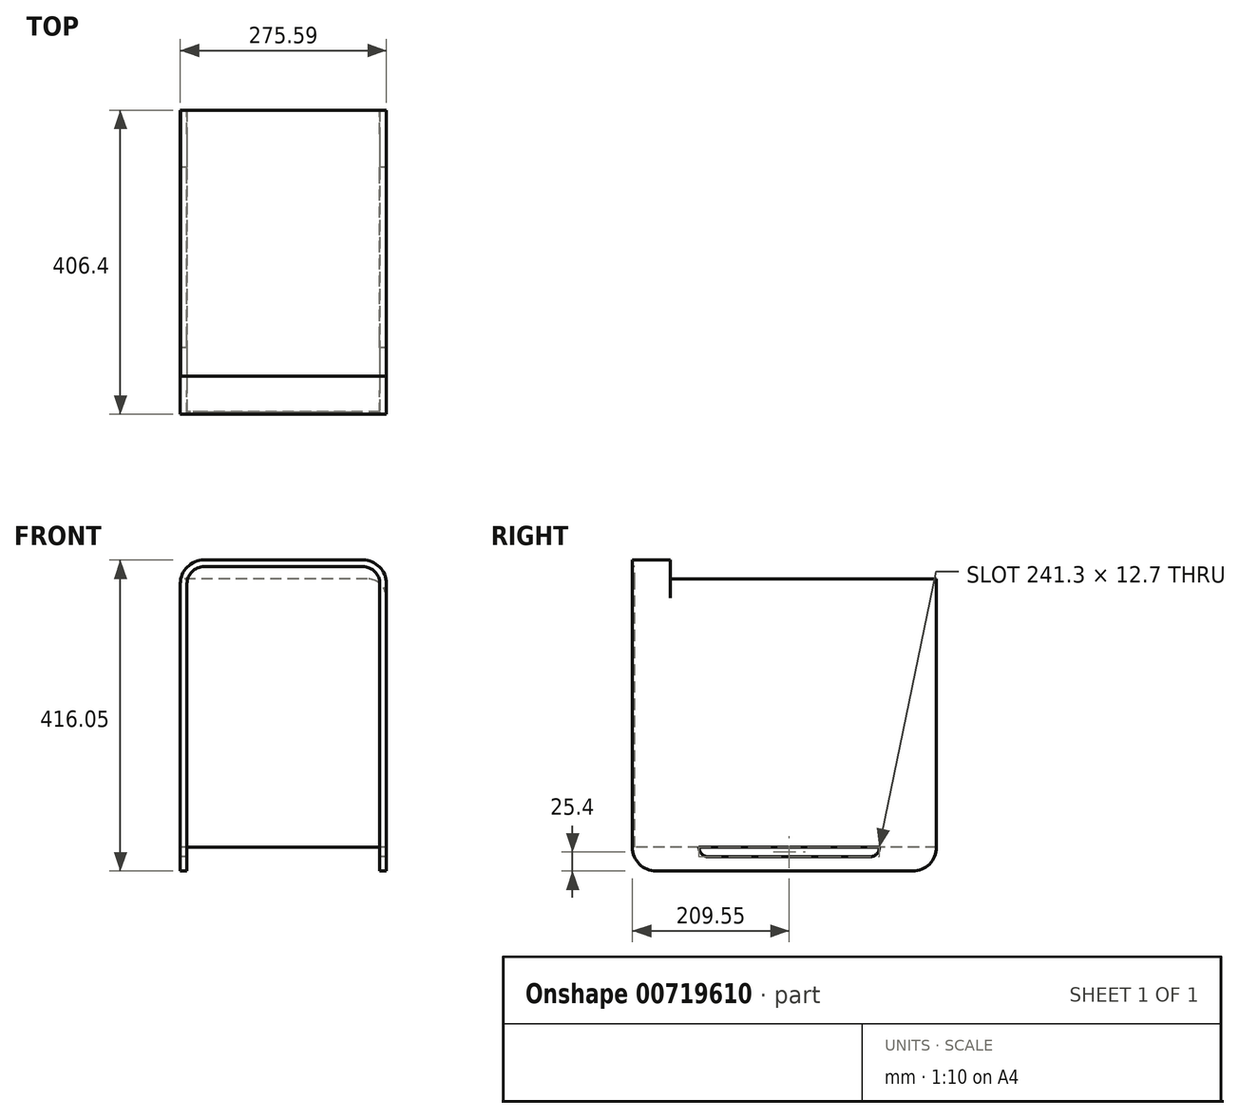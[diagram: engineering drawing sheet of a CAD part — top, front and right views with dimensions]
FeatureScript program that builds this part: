
annotation { "Feature Type Name" : "Feature", "Feature Type Description" : "" }
export const myFeature = defineFeature(function(context is Context, id is Id, definition is map)
    precondition{}
    {
        {
            var Q0;
            Q0=qCreatedBy(makeId("Front.planeOp"),FACE);
            var sketch = newSketch(context, id + "F0", { "sketchPlane" : qUnion([Q0])});
            skLineSegment(sketch, "E0.bottom", {"start": v(0, 0) * mm, "end": v(275.59, 0) * mm});
            skLineSegment(sketch, "E0.top", {"start": v(0, 416.05) * mm, "end": v(275.59, 416.05) * mm});
            skLineSegment(sketch, "E0.left", {"start": v(0, 0) * mm, "end": v(0, 416.05) * mm});
            skLineSegment(sketch, "E0.right", {"start": v(275.59, 0) * mm, "end": v(275.59, 416.05) * mm});
            skSolve(sketch);
        }
        {
            var Q0;
            Q0 = qSketchRegion(id + "F0", true);
            extrude(context, id + "F1", {"entities" : qUnion([Q0]), "oppositeDirection" : true, "depth" : 406.4 * mm, "offsetDistance" : 25.4 * mm});
        }
        {
            var Q0;
            Q0=makeQuery(id+"F1.opExtrude","CAP_FACE",FACE,{"disambiguationData":[OSD([sQuery(id+"F0.wireOp",EDGE,"E0.bottom"),sQuery(id+"F0.wireOp",EDGE,"E0.top"),sQuery(id+"F0.wireOp",EDGE,"E0.left"),sQuery(id+"F0.wireOp",EDGE,"E0.right")])],"isStart":true});
            var sketch = newSketch(context, id + "F2", { "sketchPlane" : qUnion([Q0])});
            skLineSegment(sketch, "E1", {"start": v(137.8, 416.05) * mm, "end": v(137.8, 0) * mm, "construction": true});
            skLineSegment(sketch, "E2", {"start": v(8.9, 0) * mm, "end": v(8.89, 31.75) * mm});
            skLineSegment(sketch, "E3", {"start": v(8.89, 31.75) * mm, "end": v(137.8, 31.75) * mm});
            skLineSegment(sketch, "E4", {"start": v(8.89, 0) * mm, "end": v(137.8, 0) * mm});
            skLineSegment(sketch, "E5.MirrorCS", {"start": v(266.7, 31.75) * mm, "end": v(137.8, 31.75) * mm});
            skLineSegment(sketch, "E6.MirrorCS", {"start": v(266.7, 0) * mm, "end": v(266.7, 31.75) * mm});
            skLineSegment(sketch, "E7.MirrorCS", {"start": v(266.7, 0) * mm, "end": v(137.8, 0) * mm});
            skSolve(sketch);
        }
        {
            var Q0;
            Q0 = qSketchRegion(id + "F2", true);
            extrude(context, id + "F3", {"entities" : qUnion([Q0]), "operationType" : NewBodyOperationType.REMOVE, "endBound" : BoundingType.THROUGH_ALL, "oppositeDirection" : true, "depth" : 25.4 * mm, "offsetDistance" : 25.4 * mm});
        }
        {
            var Q0;
            Q0=makeQuery(id+"F1.opExtrude","SWEPT_FACE",FACE,{"disambiguationData":[OSD([sQuery(id+"F0.wireOp",EDGE,"E0.left")])]});
            var sketch = newSketch(context, id + "F4", { "sketchPlane" : qUnion([Q0])});
            skLineSegment(sketch, "E8", {"start": v(-406.4, 390.65) * mm, "end": v(-50.8, 390.65) * mm});
            skLineSegment(sketch, "E9", {"start": v(-50.8, 390.65) * mm, "end": v(-50.8, 416.05) * mm});
            skLineSegment(sketch, "E10", {"start": v(-50.8, 416.05) * mm, "end": v(-406.4, 416.05) * mm});
            skLineSegment(sketch, "E11", {"start": v(-406.4, 416.05) * mm, "end": v(-406.4, 390.65) * mm});
            skLineSegment(sketch, "E12", {"start": v(-317.5, 19.05) * mm, "end": v(-101.6, 19.05) * mm});
            skLineSegment(sketch, "E13", {"start": v(-330.2, 31.75) * mm, "end": v(-88.9, 31.75) * mm});
            skLineSegment(sketch, "E14", {"start": v(-88.9, 31.75) * mm, "end": v(-88.9, 31.75) * mm});
            skLineSegment(sketch, "E15", {"start": v(-330.2, 31.75) * mm, "end": v(-330.2, 31.75) * mm});
            skPoint(sketch, "E16.visualSharp", {"position": v(-88.9, 19.05) * mm});
            skArc(sketch, "E16.filletArc", {"start": v(-101.6, 19.05) * mm, "mid": v(-92.62, 22.77) * mm, "end": v(-88.9, 31.75) * mm});
            skPoint(sketch, "E17.visualSharp", {"position": v(-330.2, 19.05) * mm});
            skArc(sketch, "E17.filletArc", {"start": v(-330.2, 31.75) * mm, "mid": v(-326.48, 22.77) * mm, "end": v(-317.5, 19.05) * mm});
            skSolve(sketch);
        }
        {
            var Q0;
            Q0=makeQuery(id+"F4.imprint","IMPRINT",FACE,{"disambiguationData":[TD([[makeQuery(id+"F4.imprint","IMPRINT",EDGE,{"derivedFrom":sQuery(id+"F4.wireOp",EDGE,"E8")}),1.0]])]});
            var Q1;
            Q1=makeQuery(id+"F4.imprint","IMPRINT",FACE,{"disambiguationData":[TD([[makeQuery(id+"F4.imprint","IMPRINT",EDGE,{"derivedFrom":sQuery(id+"F4.wireOp",EDGE,"E12")}),1.0]])]});
            extrude(context, id + "F5", {"entities" : qUnion([Q0, Q1]), "operationType" : NewBodyOperationType.REMOVE, "endBound" : BoundingType.THROUGH_ALL, "oppositeDirection" : true, "depth" : 25.4 * mm, "offsetDistance" : 25.4 * mm});
        }
        {
            var Q0;
            {var subQ0=sQuery(id+"F0.wireOp",EDGE,"E0.bottom");var subQ1=sQuery(id+"F0.wireOp",EDGE,"E0.left");Q0=makeQuery(id+"F3.boolean.opBoolean","SPLIT",EDGE,{"disambiguationData":[TD([makeQuery(id+"F1.opExtrude","SWEPT_FACE",FACE,{"disambiguationData":[OSD([subQ1])]})])],"derivedFrom":makeQuery(id+"F1.opExtrude","CAP_EDGE",EDGE,{"disambiguationData":[OSD([subQ0])],"isStart":false})});}
            var Q1;
            {var subQ0=sQuery(id+"F0.wireOp",EDGE,"E0.bottom");var subQ1=sQuery(id+"F0.wireOp",EDGE,"E0.right");Q1=makeQuery(id+"F3.boolean.opBoolean","SPLIT",EDGE,{"disambiguationData":[TD([makeQuery(id+"F1.opExtrude","SWEPT_FACE",FACE,{"disambiguationData":[OSD([subQ1])]})])],"derivedFrom":makeQuery(id+"F1.opExtrude","CAP_EDGE",EDGE,{"disambiguationData":[OSD([subQ0])],"isStart":false})});}
            var Q2;
            {var subQ0=sQuery(id+"F0.wireOp",EDGE,"E0.bottom");var subQ1=sQuery(id+"F0.wireOp",EDGE,"E0.left");Q2=makeQuery(id+"F3.boolean.opBoolean","SPLIT",EDGE,{"disambiguationData":[TD([makeQuery(id+"F1.opExtrude","SWEPT_FACE",FACE,{"disambiguationData":[OSD([subQ1])]})])],"derivedFrom":makeQuery(id+"F1.opExtrude","CAP_EDGE",EDGE,{"disambiguationData":[OSD([subQ0])],"isStart":true})});}
            var Q3;
            {var subQ0=sQuery(id+"F0.wireOp",EDGE,"E0.bottom");var subQ1=sQuery(id+"F0.wireOp",EDGE,"E0.right");Q3=makeQuery(id+"F3.boolean.opBoolean","SPLIT",EDGE,{"disambiguationData":[TD([makeQuery(id+"F1.opExtrude","SWEPT_FACE",FACE,{"disambiguationData":[OSD([subQ1])]})])],"derivedFrom":makeQuery(id+"F1.opExtrude","CAP_EDGE",EDGE,{"disambiguationData":[OSD([subQ0])],"isStart":true})});}
            fillet(context, id + "F6", {"entities" : qUnion([Q0, Q1, Q2, Q3]), "radius" : 31.75 * mm, "tangentPropagation" : true, "allowEdgeOverflow" : false});
        }
        {
            var Q0;
            Q0=makeQuery(id+"F5.boolean.opBoolean","COPY",EDGE,{"derivedFrom":makeQuery(id+"F5.opExtrude","CAP_EDGE",EDGE,{"disambiguationData":[OSD([sQuery(id+"F4.wireOp",EDGE,"E8")])],"isStart":true})});
            var Q1;
            Q1=makeQuery(id+"F5.boolean.opBoolean","INTERSECT",EDGE,{"derivedFrom":[makeQuery(id+"F1.opExtrude","SWEPT_FACE",FACE,{"disambiguationData":[OSD([sQuery(id+"F0.wireOp",EDGE,"E0.right")])]}),makeQuery(id+"F5.opExtrude","SWEPT_FACE",FACE,{"disambiguationData":[OSD([sQuery(id+"F4.wireOp",EDGE,"E8")])]})]});
            fillet(context, id + "F7", {"entities" : qUnion([Q0, Q1]), "radius" : 25.4 * mm, "tangentPropagation" : true, "allowEdgeOverflow" : false});
        }
        {
            var Q0;
            Q0=makeQuery(id+"F1.opExtrude","SWEPT_EDGE",EDGE,{"disambiguationData":[OSD([sQuery(id+"F0.wireOp",EDGE,"E0.top"),sQuery(id+"F0.wireOp",EDGE,"E0.right")])]});
            var Q1;
            Q1=makeQuery(id+"F1.opExtrude","SWEPT_EDGE",EDGE,{"disambiguationData":[OSD([sQuery(id+"F0.wireOp",EDGE,"E0.top"),sQuery(id+"F0.wireOp",EDGE,"E0.left")])]});
            fillet(context, id + "F8", {"entities" : qUnion([Q0, Q1]), "radius" : 31.75 * mm, "tangentPropagation" : true, "allowEdgeOverflow" : false});
        }
        {
            var Q0;
            Q0=makeQuery(id+"F1.opExtrude","CAP_FACE",FACE,{"disambiguationData":[OSD([sQuery(id+"F0.wireOp",EDGE,"E0.bottom"),sQuery(id+"F0.wireOp",EDGE,"E0.top"),sQuery(id+"F0.wireOp",EDGE,"E0.left"),sQuery(id+"F0.wireOp",EDGE,"E0.right")])],"isStart":true});
            var sketch = newSketch(context, id + "F9", { "sketchPlane" : qUnion([Q0])});
            skLineSegment(sketch, "E18.0", {"start": v(8.89, 31.75) * mm, "end": v(8.89, 384.3) * mm});
            skLineSegment(sketch, "E18.1", {"start": v(266.7, 31.75) * mm, "end": v(266.7, 384.3) * mm});
            skArc(sketch, "E18.2", {"start": v(266.7, 384.3) * mm, "mid": v(260, 400.47) * mm, "end": v(243.84, 407.16) * mm});
            skLineSegment(sketch, "E18.3", {"start": v(31.75, 407.16) * mm, "end": v(243.84, 407.16) * mm});
            skArc(sketch, "E18.4", {"start": v(31.75, 407.16) * mm, "mid": v(15.59, 400.47) * mm, "end": v(8.89, 384.3) * mm});
            skLineSegment(sketch, "E19", {"start": v(8.9, 31.75) * mm, "end": v(266.7, 31.75) * mm});
            skSolve(sketch);
        }
        {
            var Q0;
            Q0=makeQuery(id+"F9.imprint","IMPRINT",FACE,{"disambiguationData":[TD([[makeQuery(id+"F9.imprint","IMPRINT",EDGE,{"derivedFrom":sQuery(id+"F9.wireOp",EDGE,"E18.0")}),-1.0]])]});
            extrude(context, id + "F10", {"entities" : qUnion([Q0]), "operationType" : NewBodyOperationType.REMOVE, "oppositeDirection" : true, "depth" : 3.17 * mm, "offsetDistance" : 25.4 * mm});
        }
    });
